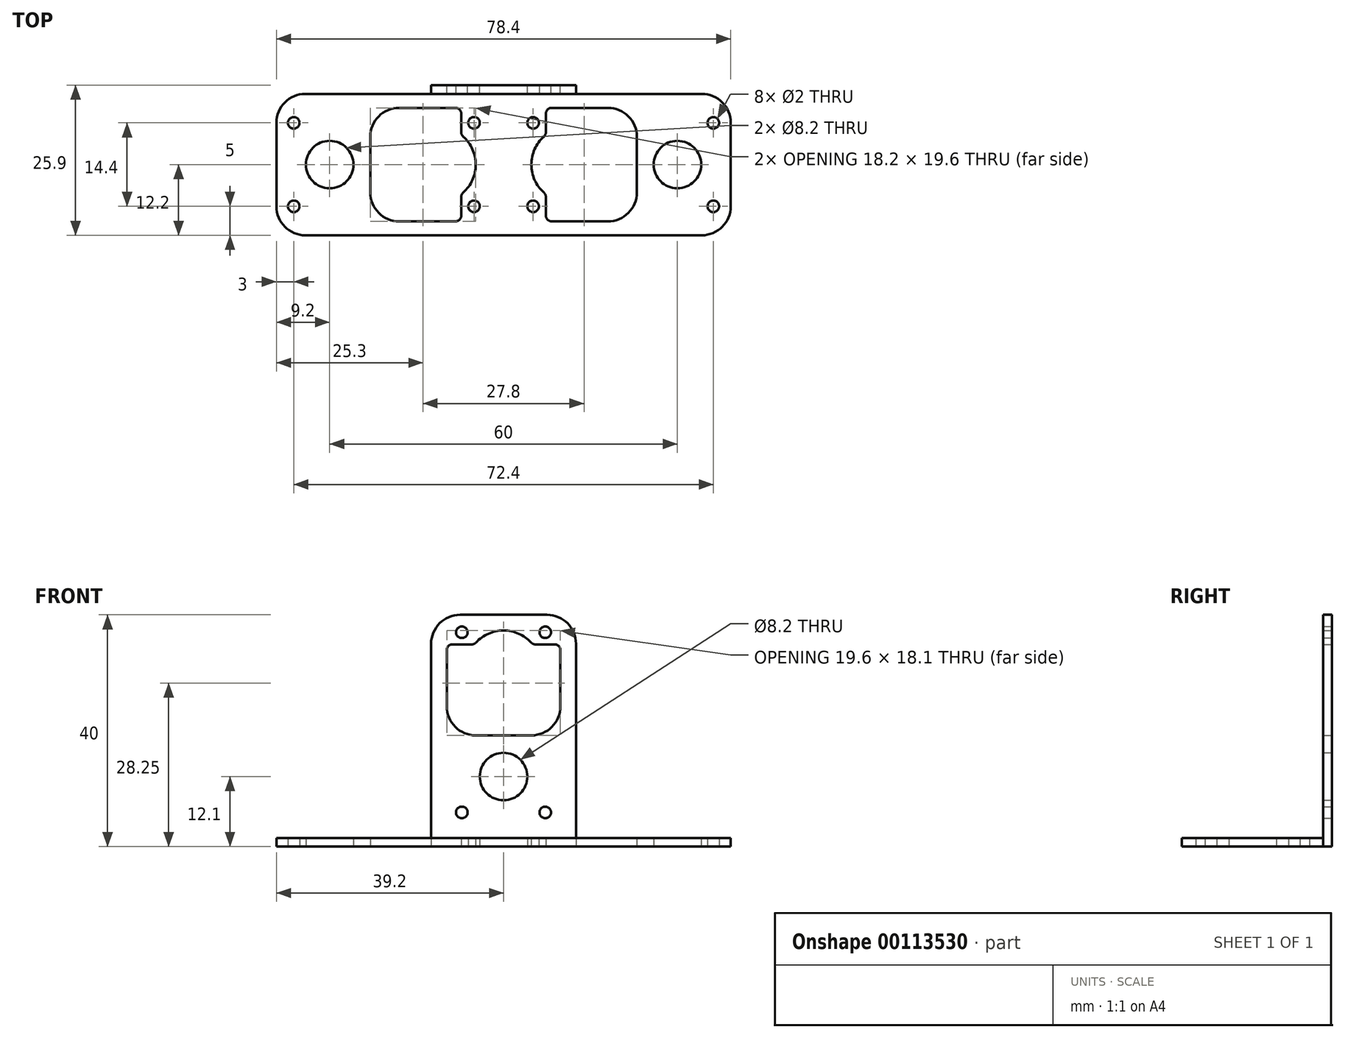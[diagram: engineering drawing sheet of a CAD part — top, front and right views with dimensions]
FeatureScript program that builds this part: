
annotation { "Feature Type Name" : "Feature", "Feature Type Description" : "" }
export const myFeature = defineFeature(function(context is Context, id is Id, definition is map)
    precondition{}
    {
        {
            var Q0;
            Q0=qCreatedBy(makeId("Top.planeOp"),FACE);
            var sketch = newSketch(context, id + "F0", { "sketchPlane" : qUnion([Q0])});
            skLineSegment(sketch, "E0.bottom", {"start": v(39.2, -12.2) * mm, "end": v(-39.2, -12.2) * mm});
            skLineSegment(sketch, "E0.top", {"start": v(39.2, 12.2) * mm, "end": v(-39.2, 12.2) * mm});
            skLineSegment(sketch, "E0.left", {"start": v(39.2, -12.2) * mm, "end": v(39.2, 12.2) * mm});
            skLineSegment(sketch, "E0.right", {"start": v(-39.2, -12.2) * mm, "end": v(-39.2, 12.2) * mm});
            skPoint(sketch, "E0.middle", {"position": v(0, 0) * mm});
            skCircle(sketch, "E1", {"center": v(-30, 0) * mm, "radius": 4.1 * mm});
            skCircle(sketch, "E2", {"center": v(-36.2, 7.2) * mm, "radius": 1 * mm});
            skCircle(sketch, "E3", {"center": v(-5.1, 7.2) * mm, "radius": 1 * mm});
            skLineSegment(sketch, "E4.bottom", {"start": v(-18, 9.8) * mm, "end": v(-8.3, 9.8) * mm});
            skLineSegment(sketch, "E4.top", {"start": v(-18, -9.8) * mm, "end": v(-8.3, -9.8) * mm});
            skLineSegment(sketch, "E4.left", {"start": v(-23, 4.8) * mm, "end": v(-23, -4.8) * mm});
            skLineSegment(sketch, "E4.right", {"start": v(-7.3, 8.8) * mm, "end": v(-7.3, 5.6) * mm});
            skPoint(sketch, "E4.middle", {"position": v(-15.15, 0) * mm});
            skPoint(sketch, "E5.visualSharp", {"position": v(-23, 9.8) * mm});
            skArc(sketch, "E5.filletArc", {"start": v(-18, 9.8) * mm, "mid": v(-21.54, 8.34) * mm, "end": v(-23, 4.8) * mm});
            skPoint(sketch, "E6.visualSharp", {"position": v(-23, -9.8) * mm});
            skArc(sketch, "E6.filletArc", {"start": v(-23, -4.8) * mm, "mid": v(-21.54, -8.34) * mm, "end": v(-18, -9.8) * mm});
            skPoint(sketch, "E7.visualSharp", {"position": v(-7.3, 9.8) * mm});
            skArc(sketch, "E7.filletArc", {"start": v(-7.3, 8.8) * mm, "mid": v(-7.6, 9.5) * mm, "end": v(-8.3, 9.8) * mm});
            skPoint(sketch, "E8.visualSharp", {"position": v(-7.3, -9.8) * mm});
            skArc(sketch, "E8.filletArc", {"start": v(-8.3, -9.8) * mm, "mid": v(-7.6, -9.5) * mm, "end": v(-7.3, -8.8) * mm});
            skCircle(sketch, "E9.MirrorC", {"center": v(-36.2, -7.2) * mm, "radius": 1 * mm});
            skCircle(sketch, "E10.MirrorC", {"center": v(-5.1, -7.2) * mm, "radius": 1 * mm});
            skArc(sketch, "E11.MirrorCS", {"start": v(7.3, 8.8) * mm, "mid": v(7.6, 9.5) * mm, "end": v(8.3, 9.8) * mm});
            skArc(sketch, "E12.MirrorCS", {"start": v(8.3, -9.8) * mm, "mid": v(7.6, -9.5) * mm, "end": v(7.3, -8.8) * mm});
            skCircle(sketch, "E13.MirrorC", {"center": v(5.1, -7.2) * mm, "radius": 1 * mm});
            skArc(sketch, "E14.MirrorCS", {"start": v(23, -4.8) * mm, "mid": v(21.54, -8.34) * mm, "end": v(18, -9.8) * mm});
            skArc(sketch, "E15.MirrorCS", {"start": v(18, 9.8) * mm, "mid": v(21.54, 8.34) * mm, "end": v(23, 4.8) * mm});
            skLineSegment(sketch, "E16.MirrorCS", {"start": v(7.3, 8.8) * mm, "end": v(7.3, 5.6) * mm});
            skPoint(sketch, "E17.MirrorP", {"position": v(7.3, -9.8) * mm});
            skLineSegment(sketch, "E18.MirrorCS", {"start": v(18, 9.8) * mm, "end": v(8.3, 9.8) * mm});
            skCircle(sketch, "E19.MirrorC", {"center": v(5.1, 7.2) * mm, "radius": 1 * mm});
            skPoint(sketch, "E20.MirrorP", {"position": v(7.3, 9.8) * mm});
            skPoint(sketch, "E21.MirrorP", {"position": v(15.15, 0) * mm});
            skCircle(sketch, "E22.MirrorC", {"center": v(36.2, -7.2) * mm, "radius": 1 * mm});
            skCircle(sketch, "E23.MirrorC", {"center": v(36.2, 7.2) * mm, "radius": 1 * mm});
            skCircle(sketch, "E24.MirrorC", {"center": v(30, 0) * mm, "radius": 4.1 * mm});
            skLineSegment(sketch, "E25.MirrorCS", {"start": v(23, 4.8) * mm, "end": v(23, -4.8) * mm});
            skPoint(sketch, "E26.MirrorP", {"position": v(23, -9.8) * mm});
            skLineSegment(sketch, "E27.MirrorCS", {"start": v(18, -9.8) * mm, "end": v(8.3, -9.8) * mm});
            skPoint(sketch, "E28.MirrorP", {"position": v(23, 9.8) * mm});
            skArc(sketch, "E29", {"start": v(-6.97, -4.84) * mm, "mid": v(-4.8, 0) * mm, "end": v(-6.97, 4.84) * mm});
            skLineSegment(sketch, "E30.trimOffspring", {"start": v(-7.3, -5.6) * mm, "end": v(-7.3, -8.8) * mm});
            skPoint(sketch, "E31.visualSharp", {"position": v(-7.3, 5.12) * mm});
            skArc(sketch, "E31.filletArc", {"start": v(-7.3, 5.6) * mm, "mid": v(-7.21, 5.18) * mm, "end": v(-6.97, 4.84) * mm});
            skPoint(sketch, "E32.visualSharp", {"position": v(-7.3, -5.12) * mm});
            skArc(sketch, "E32.filletArc", {"start": v(-6.97, -4.84) * mm, "mid": v(-7.21, -5.18) * mm, "end": v(-7.3, -5.6) * mm});
            skArc(sketch, "E33.MirrorCS", {"start": v(7.3, 5.6) * mm, "mid": v(7.21, 5.18) * mm, "end": v(6.97, 4.84) * mm});
            skArc(sketch, "E34.MirrorCS", {"start": v(6.97, -4.84) * mm, "mid": v(4.8, 0) * mm, "end": v(6.97, 4.84) * mm});
            skPoint(sketch, "E35.MirrorP", {"position": v(7.3, 5.12) * mm});
            skPoint(sketch, "E36.MirrorP", {"position": v(7.3, -5.12) * mm});
            skArc(sketch, "E37.MirrorCS", {"start": v(6.97, -4.84) * mm, "mid": v(7.21, -5.18) * mm, "end": v(7.3, -5.6) * mm});
            skLineSegment(sketch, "E38.trimOffspring", {"start": v(7.3, -5.6) * mm, "end": v(7.3, -8.8) * mm});
            skSolve(sketch);
        }
        {
            var Q0;
            Q0=qSketchRegion(id+"F0",true);
            extrude(context, id + "F1", {"entities" : qUnion([Q0]), "depth" : 1.5 * mm});
        }
        {
            var Q0;
            Q0=qCreatedBy(makeId("Top.planeOp"),FACE);
            var sketch = newSketch(context, id + "F2", { "sketchPlane" : qUnion([Q0])});
            skLineSegment(sketch, "E39.bottom", {"start": v(12.5, 12.2) * mm, "end": v(-12.5, 12.2) * mm});
            skLineSegment(sketch, "E39.top", {"start": v(12.5, 13.7) * mm, "end": v(-12.5, 13.7) * mm});
            skLineSegment(sketch, "E39.left", {"start": v(12.5, 12.2) * mm, "end": v(12.5, 13.7) * mm});
            skLineSegment(sketch, "E39.right", {"start": v(-12.5, 12.2) * mm, "end": v(-12.5, 13.7) * mm});
            skPoint(sketch, "E39.middle", {"position": v(0, 12.95) * mm});
            skLineSegment(sketch, "E40.0", {"start": v(39.2, 12.2) * mm, "end": v(-39.2, 12.2) * mm, "construction": true});
            skSolve(sketch);
        }
        {
            var Q0;
            Q0=qSketchRegion(id+"F2",true);
            extrude(context, id + "F3", {"entities" : qUnion([Q0]), "operationType" : NewBodyOperationType.ADD, "depth" : 40 * mm});
        }
        {
            var Q0;
            Q0=makeQuery(id+"F3.opExtrude","SWEPT_FACE",FACE,{"disambiguationData":[OSD([sQuery(id+"F2.wireOp",EDGE,"E39.top")])]});
            var sketch = newSketch(context, id + "F4", { "sketchPlane" : qUnion([Q0])});
            skLineSegment(sketch, "E41", {"start": v(-12.5, 20) * mm, "end": v(12.5, 20) * mm, "construction": true});
            skCircle(sketch, "E42", {"center": v(7.2, 37) * mm, "radius": 1 * mm});
            skCircle(sketch, "E43", {"center": v(7.2, 5.9) * mm, "radius": 1 * mm});
            skCircle(sketch, "E44", {"center": v(0, 12.1) * mm, "radius": 4.1 * mm});
            skLineSegment(sketch, "E45.bottom", {"start": v(8.8, 34.9) * mm, "end": v(5.5, 34.9) * mm});
            skLineSegment(sketch, "E45.top", {"start": v(4.8, 19.2) * mm, "end": v(-4.8, 19.2) * mm});
            skLineSegment(sketch, "E45.left", {"start": v(9.8, 33.9) * mm, "end": v(9.8, 24.2) * mm});
            skLineSegment(sketch, "E45.right", {"start": v(-9.8, 33.9) * mm, "end": v(-9.8, 24.2) * mm});
            skPoint(sketch, "E45.middle", {"position": v(0, 27.05) * mm});
            skPoint(sketch, "E46.visualSharp", {"position": v(-9.8, 19.2) * mm});
            skArc(sketch, "E46.filletArc", {"start": v(-9.8, 24.2) * mm, "mid": v(-8.34, 20.66) * mm, "end": v(-4.8, 19.2) * mm});
            skPoint(sketch, "E47.visualSharp", {"position": v(9.8, 19.2) * mm});
            skArc(sketch, "E47.filletArc", {"start": v(4.8, 19.2) * mm, "mid": v(8.34, 20.66) * mm, "end": v(9.8, 24.2) * mm});
            skPoint(sketch, "E48.visualSharp", {"position": v(9.8, 34.9) * mm});
            skArc(sketch, "E48.filletArc", {"start": v(9.8, 33.9) * mm, "mid": v(9.5, 34.6) * mm, "end": v(8.8, 34.9) * mm});
            skPoint(sketch, "E49.visualSharp", {"position": v(-9.8, 34.9) * mm});
            skArc(sketch, "E49.filletArc", {"start": v(-8.8, 34.9) * mm, "mid": v(-9.5, 34.6) * mm, "end": v(-9.8, 33.9) * mm});
            skCircle(sketch, "E50.MirrorC", {"center": v(-7.2, 37) * mm, "radius": 1 * mm});
            skCircle(sketch, "E51.MirrorC", {"center": v(-7.2, 5.9) * mm, "radius": 1 * mm});
            skArc(sketch, "E52", {"start": v(4.77, 35.22) * mm, "mid": v(0, 37.3) * mm, "end": v(-4.77, 35.22) * mm});
            skLineSegment(sketch, "E53.trimOffspring", {"start": v(-5.5, 34.9) * mm, "end": v(-8.8, 34.9) * mm});
            skPoint(sketch, "E54.visualSharp", {"position": v(-5.04, 34.9) * mm});
            skArc(sketch, "E54.filletArc", {"start": v(-5.5, 34.9) * mm, "mid": v(-5.1, 34.98) * mm, "end": v(-4.77, 35.22) * mm});
            skPoint(sketch, "E55.visualSharp", {"position": v(5.04, 34.9) * mm});
            skArc(sketch, "E55.filletArc", {"start": v(4.77, 35.22) * mm, "mid": v(5.1, 34.98) * mm, "end": v(5.5, 34.9) * mm});
            skSolve(sketch);
        }
        {
            var Q0;
            Q0=qSketchRegion(id+"F4",true);
            extrude(context, id + "F5", {"entities" : qUnion([Q0]), "operationType" : NewBodyOperationType.REMOVE, "endBound" : BoundingType.UP_TO_NEXT, "oppositeDirection" : true, "depth" : 25 * mm});
        }
        {
            var Q0;
            Q0=makeQuery(id+"F1.opExtrude","SWEPT_EDGE",EDGE,{"disambiguationData":[OSD([sQuery(id+"F0.wireOp",EDGE,"E0.top"),sQuery(id+"F0.wireOp",EDGE,"E0.right")])]});
            var Q1;
            Q1=makeQuery(id+"F1.opExtrude","SWEPT_EDGE",EDGE,{"disambiguationData":[OSD([sQuery(id+"F0.wireOp",EDGE,"E0.bottom"),sQuery(id+"F0.wireOp",EDGE,"E0.right")])]});
            var Q2;
            Q2=makeQuery(id+"F1.opExtrude","SWEPT_EDGE",EDGE,{"disambiguationData":[OSD([sQuery(id+"F0.wireOp",EDGE,"E0.top"),sQuery(id+"F0.wireOp",EDGE,"E0.left")])]});
            var Q3;
            Q3=makeQuery(id+"F1.opExtrude","SWEPT_EDGE",EDGE,{"disambiguationData":[OSD([sQuery(id+"F0.wireOp",EDGE,"E0.bottom"),sQuery(id+"F0.wireOp",EDGE,"E0.left")])]});
            var Q4;
            Q4=makeQuery(id+"F3.opExtrude","CAP_EDGE",EDGE,{"disambiguationData":[OSD([sQuery(id+"F2.wireOp",EDGE,"E39.right")])],"isStart":false});
            var Q5;
            Q5=makeQuery(id+"F3.opExtrude","CAP_EDGE",EDGE,{"disambiguationData":[OSD([sQuery(id+"F2.wireOp",EDGE,"E39.left")])],"isStart":false});
            fillet(context, id + "F6", {"entities" : qUnion([Q0, Q1, Q2, Q3, Q4, Q5]), "radius" : 5 * mm, "tangentPropagation" : true, "allowEdgeOverflow" : false});
        }
    });
